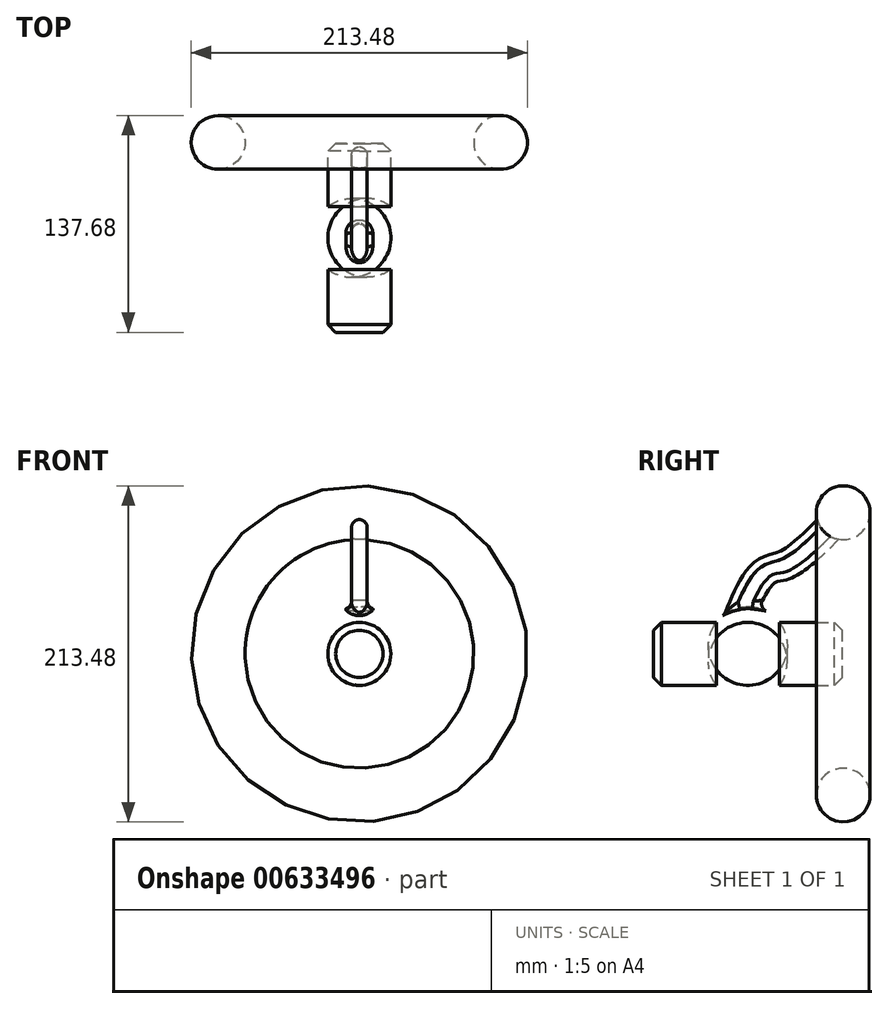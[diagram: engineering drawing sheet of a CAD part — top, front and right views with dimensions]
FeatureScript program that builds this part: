
annotation { "Feature Type Name" : "Feature", "Feature Type Description" : "" }
export const myFeature = defineFeature(function(context is Context, id is Id, definition is map)
    precondition{}
    {
        {
            var Q0;
            Q0=qCreatedBy(makeId("Top.planeOp"),FACE);
            cPlane(context, id + "F0", {"entities" : qUnion([Q0]), "cplaneType" : CPlaneType.OFFSET, "offset" : 20 * mm, "width" : 150 * mm, "height" : 150 * mm});
        }
        {
            var Q0;
            Q0=qCreatedBy(makeId("Top.planeOp"),FACE);
            var sketch = newSketch(context, id + "F1", { "sketchPlane" : qUnion([Q0])});
            skLineSegment(sketch, "E0", {"start": v(0, 66.93) * mm, "end": v(0, -53.07) * mm});
            skLineSegment(sketch, "E1", {"start": v(20, 66.93) * mm, "end": v(20, 26.93) * mm});
            skLineSegment(sketch, "E2", {"start": v(20, -13.07) * mm, "end": v(20, -53.07) * mm});
            skLineSegment(sketch, "E3", {"start": v(20, -53.07) * mm, "end": v(0, -53.07) * mm});
            skLineSegment(sketch, "E4", {"start": v(20, 66.93) * mm, "end": v(0, 66.93) * mm});
            skArc(sketch, "E5", {"start": v(20, -13.07) * mm, "mid": v(30, 6.93) * mm, "end": v(20, 26.93) * mm});
            skSolve(sketch);
        }
        {
            var Q0;
            Q0=makeQuery(id+"F1.imprint","IMPRINT",FACE,{"disambiguationData":[TD([[makeQuery(id+"F1.imprint","IMPRINT",EDGE,{"derivedFrom":sQuery(id+"F1.wireOp",EDGE,"E0")}),1.0]])]});
            var Q1;
            Q1=sQuery(id+"F1.wireOp",EDGE,"E0");
            revolve(context, id + "F2", {"entities" : qUnion([Q0]), "axis" : qUnion([Q1]), "revolveType" : RevolveType.FULL});
        }
        {
            var Q0;
            Q0=makeQuery(id+"F2.opRevolve","SWEPT_EDGE",EDGE,{"disambiguationData":[OSD([sQuery(id+"F1.wireOp",EDGE,"E1"),sQuery(id+"F1.wireOp",EDGE,"E4")])]});
            var Q1;
            Q1=makeQuery(id+"F2.opRevolve","SWEPT_EDGE",EDGE,{"disambiguationData":[OSD([sQuery(id+"F1.wireOp",EDGE,"E2"),sQuery(id+"F1.wireOp",EDGE,"E3")])]});
            chamfer(context, id + "F3", {"entities" : qUnion([Q0, Q1]), "width" : 5 * mm, "tangentPropagation" : true});
        }
        {
            var Q0;
            Q0=qCreatedBy(id+"F0.planeOp",FACE);
            var sketch = newSketch(context, id + "F4", { "sketchPlane" : qUnion([Q0])});
            skLineSegment(sketch, "E6.bottom", {"start": v(-5, 10) * mm, "end": v(5, 10) * mm});
            skLineSegment(sketch, "E6.top", {"start": v(-5, -10) * mm, "end": v(5, -10) * mm});
            skLineSegment(sketch, "E6.left", {"start": v(-5, 10) * mm, "end": v(-5, -10) * mm});
            skLineSegment(sketch, "E6.right", {"start": v(5, 10) * mm, "end": v(5, -10) * mm});
            skSolve(sketch);
        }
        {
            var Q0;
            Q0=qCreatedBy(makeId("Right.planeOp"),FACE);
            var sketch = newSketch(context, id + "F5", { "sketchPlane" : qUnion([Q0])});
            skFitSpline(sketch, "E7", {"points": [v(0, 20) * mm, v(16.95, 50.82) * mm, v(32.26, 57.5) * mm, v(66.27, 87.72) * mm], "startDerivative": vector(44.6, 108.27) * mm, "endDerivative": vector(90.58, 94.48) * mm});
            skSolve(sketch);
        }
        {
            var Q0;
            Q0 = qSketchRegion(id + "F4", true);
            var Q1;
            Q1=sQuery(id+"F5.wireOp",EDGE,"E7");
            sweep(context, id + "F6", {"operationType" : NewBodyOperationType.ADD, "profiles" : qUnion([Q0]), "path" : qUnion([Q1])});
        }
        {
            var Q0;
            Q0=makeQuery(id+"F6.opSweep","SWEPT_EDGE",EDGE,{"disambiguationData":[OSD([sQuery(id+"F4.wireOp",EDGE,"E6.bottom"),sQuery(id+"F4.wireOp",EDGE,"E6.left"),sQuery(id+"F5.wireOp",EDGE,"E7")])]});
            var Q1;
            Q1=makeQuery(id+"F6.opSweep","SWEPT_EDGE",EDGE,{"disambiguationData":[OSD([sQuery(id+"F4.wireOp",EDGE,"E6.top"),sQuery(id+"F4.wireOp",EDGE,"E6.left"),sQuery(id+"F5.wireOp",EDGE,"E7")])]});
            var Q2;
            Q2=makeQuery(id+"F6.opSweep","SWEPT_EDGE",EDGE,{"disambiguationData":[OSD([sQuery(id+"F4.wireOp",EDGE,"E6.top"),sQuery(id+"F4.wireOp",EDGE,"E6.right"),sQuery(id+"F5.wireOp",EDGE,"E7")])]});
            var Q3;
            Q3=makeQuery(id+"F6.opSweep","SWEPT_EDGE",EDGE,{"disambiguationData":[OSD([sQuery(id+"F4.wireOp",EDGE,"E6.bottom"),sQuery(id+"F4.wireOp",EDGE,"E6.right"),sQuery(id+"F5.wireOp",EDGE,"E7")])]});
            fillet(context, id + "F7", {"entities" : qUnion([Q0, Q1, Q2, Q3]), "radius" : 5 * mm, "tangentPropagation" : true, "allowEdgeOverflow" : false});
        }
        {
            var Q0;
            Q0=makeQuery(id+"F6.boolean.opBoolean","INTERSECT",EDGE,{"derivedFrom":[makeQuery(id+"F2.opRevolve","SWEPT_FACE",FACE,{"disambiguationData":[OSD([sQuery(id+"F1.wireOp",EDGE,"E5")])]}),makeQuery(id+"F6.opSweep","SWEPT_FACE",FACE,{"disambiguationData":[OSD([sQuery(id+"F4.wireOp",EDGE,"E6.right"),sQuery(id+"F5.wireOp",EDGE,"E7")])]})]});
            fillet(context, id + "F8", {"entities" : qUnion([Q0]), "radius" : 5 * mm, "tangentPropagation" : true, "allowEdgeOverflow" : false});
        }
        {
            var Q0;
            Q0=qCreatedBy(makeId("Right.planeOp"),FACE);
            var sketch = newSketch(context, id + "F9", { "sketchPlane" : qUnion([Q0])});
            skCircle(sketch, "E8", {"center": v(67.56, 89.7) * mm, "radius": 17.04 * mm});
            skSolve(sketch);
        }
        {
            var Q0;
            Q0 = qSketchRegion(id + "F9", true);
            var Q1;
            Q1=makeQuery(id+"F2.opRevolve","SWEPT_FACE",FACE,{"disambiguationData":[OSD([sQuery(id+"F1.wireOp",EDGE,"E1")])]});
            revolve(context, id + "F10", {"operationType" : NewBodyOperationType.ADD, "entities" : qUnion([Q0]), "axis" : qUnion([Q1]), "revolveType" : RevolveType.FULL});
        }
    });
